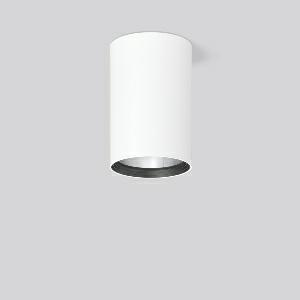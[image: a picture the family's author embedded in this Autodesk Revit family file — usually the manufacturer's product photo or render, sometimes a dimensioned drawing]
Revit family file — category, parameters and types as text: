
# Revit family: heledon_maxi_a_931216_002_0f04
name_source: partatom
category: Lighting Fixtures
units: mm (PartAtom-declared; Revit-internal decimal feet)

## family parameters
Cut with Voids When Loaded = No
Host = Face
Light Source = No
Part Type = Normal
Room Calculation Point = No
Round Connector Dimension = Use Diameter
Shared = No

## types (1)
- HELEDON maxi A (1 x LED Modul 930, 3250 lm, 3000)
    Apparent Load = 25 VA
    Approval mark = CE
    CIE Flux Codes = 100 100 100 100 100
    Color Rendering = 90
    Color Temperature = 3000
    Default Elevation = 1800 mm
    Description = Series: HELEDON maxi
Cylindrical surface-mounted downlight. Housing: die-cast aluminium, powder-coated. Internal ceiling frame polycarbonate with bayonet mounting. Black plastic ring and recessed LED to prevent glare from the side. Optical assembly with reflector made of MIRO-Silver with 98% total light reflection for outstanding efficiency - can be changed without tools. Best colour rendering index Ra>90. Suitable for Ceiling mounting. Easy installation with a separate ceiling frame with bayonet mounting and plug connection. Driver integrated. Connected via plug-in connector. High quality converter without flickering and stroboscopic effect. The following accessories can be mounted without use of tools: interchangeable lenses, decorative glasses, honeycomb louvre, clear and frosted diffusers, white interchangeable plastic ring. 
Colour: traffic white, matt (RAL 9016)
Diameter: 123 mm
Height: 183 mm
Lamp: LED
Socket: without socket
Colour temperature: 3000K
Colour rendering index (CRI): 92
System power: 25 W
Rated luminous flux: 3250 lm
Luminous efficiency: 130 lm/W
Control gear: Regulated power supply
Protection class: I
Type of protection: IP 20
    Height = 183 mm
    Lamp = 1 x LED Modul 930
    Lamp Light Flux = 3250 lm
    Lamp count = 1
    Length = 123 mm
    Lifetime = 50000 h
    Luminous efficacy = 130 lm/W
    Manufacturer = RZB
    ModVariant = No
    Model = 931216.002
    Mounting Place = Ceiling
    Mounting Type = Surface mounted
    Number of Poles = 1
    OnlyDefault = Yes
    Power Factor = 1
    Product Name = HELEDON maxi A
    Product group = Surface mounted downlights
    ProductGroupID = 302
    Protection Class = Protection class I
    Protection Degree = IP 20
    RLX_Detail_Level = 1
    RLX_Emergency_Light_Flux = 0 lm
    RLX_Emergency_Type = 0
    RLX_Emergency_Type_DB = No
    RlxData = <blob elided: 96201 chars, md5=f7f37e24>
    Socket = socket
    Standby Power = 0 W
    System Light Flux = 3250 lm
    System Power = 25 W
    Type Comments = Product without accessories
    Type Image = 931192.002.jpg
    URL = http://relux.com
    VarID = ---
    Voltage = 230 V
    Voltage Range = 220-240 V
    Weight = 0.00 kg
    Width = 0 mm  [stored 0 ft]

note: [stored X ft] marks values corroborated as IEEE doubles in the binary element streams (Revit-internal decimal feet)

## geometry (parser evidence)
native form markers: Blend x4, Sweep x10
no freeform markers — native parametric forms only
